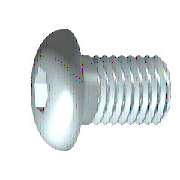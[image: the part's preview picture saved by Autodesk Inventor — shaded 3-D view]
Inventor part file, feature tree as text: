
AUTODESK INVENTOR PART (.ipt)
format: ipt  version: 2012 (Build 160160000, 160)  size: 202,752 bytes
history: native  units: mm (DEFAULTED — no unit token found)
features: extrude x1, plane x1, fillet x1
ambient origin geometry x7: Origin, YZ Plane, XY Plane, X Axis, Y Axis, Z Axis, Center Point
bodies: Solid1 (feature_tree), Body (feature_tree)
feature tree (3):
  extrude  "Slot"  Depth=6.34726mm
  plane  "Work Plane1"
  fillet  "Fillet2"  Radius=1.59014mm
